# Revit family: Sense-allas vauvanhoitotasolla
name_source: partatom
category: Plumbing Fixtures
units: mm (PartAtom-declared; Revit-internal decimal feet)

## family parameters
Always vertical = Yes
Cut with Voids When Loaded = No
Maintain Annotation Orientation = No
Part Type = Normal
Room Calculation Point = No
Round Connector Dimension = Use Diameter
Shared = No
Work Plane-Based = No

## types (2) — shared parameters
Accent Colour = Composite - White
Colour = Composite - White
Depth = 640 mm  [stored 2.09974 ft]
Manufacturer = Väinö Korpinen Oy
Model = 62010 Sense-allas vauvanhoitotasolla
URL = https://www.korpinen.com
Width = 1200 mm  [stored 3.93701 ft]
zero-valued in all types: Default Elevation, NominalDepth, NominalHeight, NominalWidth

## per-type parameters (varying)
| type | Left handed | Right handed |
| 62010R - Right | No | Yes |
| 62010L - Left | Yes | No |

note: [stored X ft] marks values corroborated as IEEE doubles in the binary element streams (Revit-internal decimal feet)

## geometry (parser evidence)
native form markers: Sweep x18
no freeform markers — native parametric forms only
